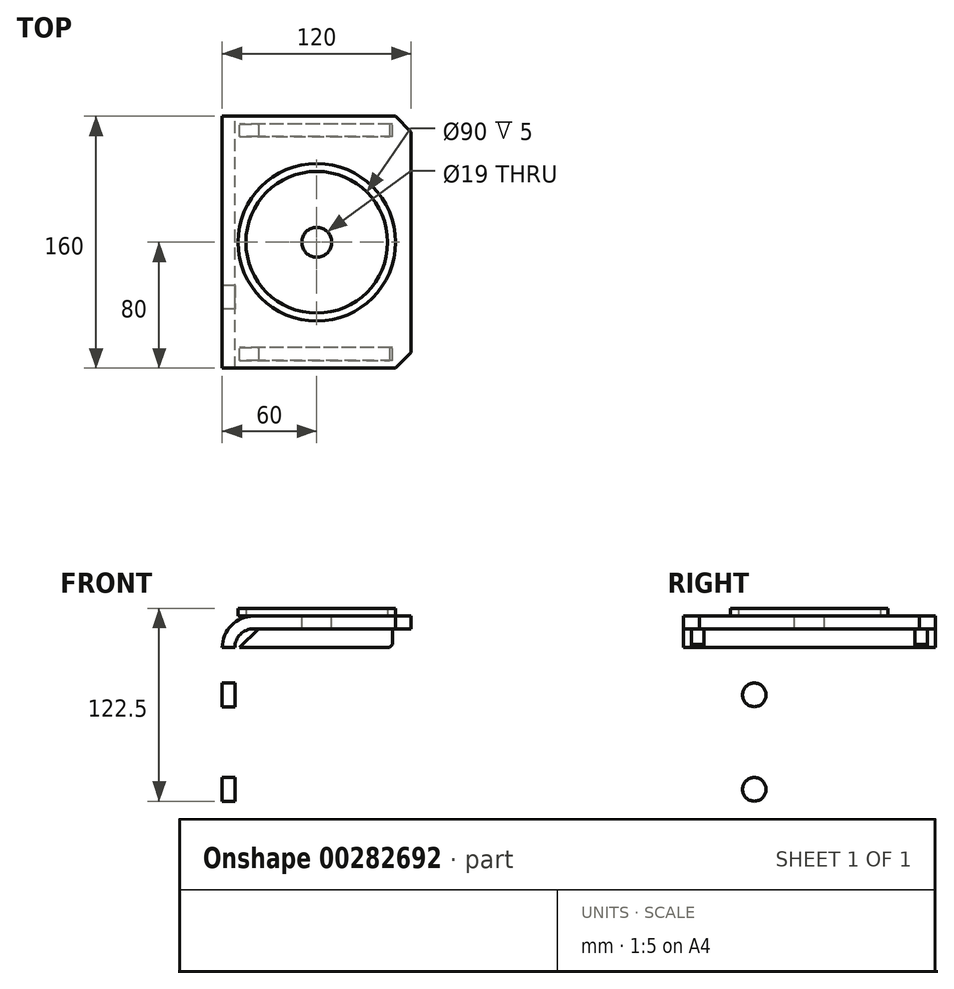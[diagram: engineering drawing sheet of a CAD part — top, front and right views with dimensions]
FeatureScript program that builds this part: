
annotation { "Feature Type Name" : "Feature", "Feature Type Description" : "" }
export const myFeature = defineFeature(function(context is Context, id is Id, definition is map)
    precondition{}
    {
        {
            var Q0;
            Q0=qCreatedBy(makeId("Front.planeOp"),FACE);
            var sketch = newSketch(context, id + "F0", { "sketchPlane" : qUnion([Q0])});
            skLineSegment(sketch, "E0", {"start": v(0, 0) * mm, "end": v(0, 120) * mm});
            skLineSegment(sketch, "E1", {"start": v(20, 140) * mm, "end": v(120, 140) * mm});
            skLineSegment(sketch, "E2.0", {"start": v(20, 132) * mm, "end": v(120, 132) * mm});
            skLineSegment(sketch, "E2.1", {"start": v(8, 0) * mm, "end": v(8, 120) * mm});
            skLineSegment(sketch, "E3", {"start": v(120, 140) * mm, "end": v(120, 132) * mm});
            skLineSegment(sketch, "E4", {"start": v(0, 0) * mm, "end": v(8, 0) * mm});
            skPoint(sketch, "E5.visualSharp", {"position": v(8, 132) * mm});
            skArc(sketch, "E5.filletArc", {"start": v(20, 132) * mm, "mid": v(11.51, 128.49) * mm, "end": v(8, 120) * mm});
            skPoint(sketch, "E6.visualSharp", {"position": v(0, 140) * mm});
            skArc(sketch, "E6.filletArc", {"start": v(20, 140) * mm, "mid": v(5.86, 134.14) * mm, "end": v(0, 120) * mm});
            skSolve(sketch);
        }
        {
            var Q0;
            Q0=makeQuery(id+"F0.imprint","IMPRINT",FACE,{"disambiguationData":[TD([[makeQuery(id+"F0.imprint","IMPRINT",EDGE,{"derivedFrom":sQuery(id+"F0.wireOp",EDGE,"E0")}),-1.0]])]});
            extrude(context, id + "F1", {"entities" : qUnion([Q0]), "depth" : 160 * mm, "symmetric" : true});
        }
        {
            var Q0;
            Q0=makeQuery(id+"F1.opExtrude","SWEPT_FACE",FACE,{"disambiguationData":[OSD([sQuery(id+"F0.wireOp",EDGE,"E2.1")])]});
            var sketch = newSketch(context, id + "F2", { "sketchPlane" : qUnion([Q0])});
            skLineSegment(sketch, "E7.0", {"start": v(-75, 132) * mm, "end": v(-67, 132) * mm});
            skLineSegment(sketch, "E8", {"start": v(-75, 132) * mm, "end": v(-75, 12) * mm});
            skLineSegment(sketch, "E9", {"start": v(-75, 12) * mm, "end": v(-67, 12) * mm});
            skLineSegment(sketch, "E10", {"start": v(-67, 12) * mm, "end": v(-67, 132) * mm});
            skLineSegment(sketch, "E11", {"start": v(67, 132) * mm, "end": v(67, 12) * mm});
            skLineSegment(sketch, "E12", {"start": v(67, 12) * mm, "end": v(75, 12) * mm});
            skLineSegment(sketch, "E13", {"start": v(75, 12) * mm, "end": v(75, 132) * mm});
            skPoint(sketch, "E14.orphan", {"position": v(-80, 132) * mm});
            skLineSegment(sketch, "E15.trimOffspring", {"start": v(67, 132) * mm, "end": v(75, 132) * mm});
            skPoint(sketch, "E16.orphan", {"position": v(80, 132) * mm});
            skSolve(sketch);
        }
        {
            var Q0;
            {var subQ0=sQuery(id+"F2.wireOp",EDGE,"E9");Q0=makeQuery(id+"F2.imprint","IMPRINT",FACE,{"disambiguationData":[TD([[makeQuery(id+"F2.imprint","IMPRINT",EDGE,{"derivedFrom":subQ0}),1.0]])]});}
            var Q1;
            {var subQ0=sQuery(id+"F2.wireOp",EDGE,"E12");Q1=makeQuery(id+"F2.imprint","IMPRINT",FACE,{"disambiguationData":[TD([[makeQuery(id+"F2.imprint","IMPRINT",EDGE,{"derivedFrom":subQ0}),1.0]])]});}
            var Q2;
            {var subQ0=sQuery(id+"F2.wireOp",EDGE,"E7.0");Q2=makeQuery(id+"F2.imprint","IMPRINT",FACE,{"disambiguationData":[TD([[makeQuery(id+"F2.imprint","IMPRINT",EDGE,{"derivedFrom":subQ0}),-1.0]])]});}
            var Q3;
            {var subQ0=sQuery(id+"F2.wireOp",EDGE,"E15.trimOffspring");Q3=makeQuery(id+"F2.imprint","IMPRINT",FACE,{"disambiguationData":[TD([[makeQuery(id+"F2.imprint","IMPRINT",EDGE,{"derivedFrom":subQ0}),-1.0]])]});}
            extrude(context, id + "F3", {"entities" : qUnion([Q0, Q1, Q2, Q3]), "depth" : 100 * mm});
        }
        {
            var Q0;
            Q0=makeQuery(id+"F3.opExtrude","CAP_EDGE",EDGE,{"disambiguationData":[OSD([sQuery(id+"F2.wireOp",EDGE,"E15.trimOffspring")])],"isStart":true});
            var Q1;
            Q1=makeQuery(id+"F3.opExtrude","CAP_EDGE",EDGE,{"disambiguationData":[OSD([sQuery(id+"F2.wireOp",EDGE,"E7.0")])],"isStart":true});
            chamfer(context, id + "F4", {"entities" : qUnion([Q0, Q1]), "width" : 15 * mm, "tangentPropagation" : true});
        }
        {
            var Q0;
            Q0=makeQuery(id+"F3.opExtrude","SWEPT_FACE",FACE,{"disambiguationData":[OSD([sQuery(id+"F2.wireOp",EDGE,"E13")])]});
            var sketch = newSketch(context, id + "F5", { "sketchPlane" : qUnion([Q0])});
            skLineSegment(sketch, "E17", {"start": v(-108, 122) * mm, "end": v(-18, 12) * mm});
            skSolve(sketch);
        }
        {
            var Q0;
            {var subQ0=sQuery(id+"F5.wireOp",EDGE,"E17");Q0=makeQuery(id+"F5.imprint","IMPRINT",FACE,{"disambiguationData":[TD([[makeQuery(id+"F5.imprint","IMPRINT",EDGE,{"derivedFrom":subQ0}),-1.0]])]});}
            extrude(context, id + "F6", {"entities" : qUnion([Q0]), "operationType" : NewBodyOperationType.REMOVE, "endBound" : BoundingType.THROUGH_ALL, "oppositeDirection" : true, "depth" : 25 * mm});
        }
        {
            var Q0;
            Q0=makeQuery(id+"F1.opExtrude","SWEPT_FACE",FACE,{"disambiguationData":[OSD([sQuery(id+"F0.wireOp",EDGE,"E1")])]});
            var sketch = newSketch(context, id + "F7", { "sketchPlane" : qUnion([Q0])});
            skLineSegment(sketch, "E18", {"start": v(0, 0) * mm, "end": v(154.98, 0) * mm, "construction": true});
            skPoint(sketch, "E18.endSnap0", {"position": v(20, 0) * mm});
            skCircle(sketch, "E19", {"center": v(60, 0) * mm, "radius": 9.5 * mm});
            skCircle(sketch, "E20", {"center": v(60, 0) * mm, "radius": 45 * mm});
            skCircle(sketch, "E21", {"center": v(60, 0) * mm, "radius": 50 * mm});
            skSolve(sketch);
        }
        {
            var Q0;
            Q0=makeQuery(id+"F7.imprint","IMPRINT",FACE,{"disambiguationData":[TD([[makeQuery(id+"F7.imprint","IMPRINT",EDGE,{"derivedFrom":sQuery(id+"F7.wireOp",EDGE,"E19")}),1.0]])]});
            extrude(context, id + "F8", {"entities" : qUnion([Q0]), "operationType" : NewBodyOperationType.REMOVE, "endBound" : BoundingType.THROUGH_ALL, "oppositeDirection" : true, "depth" : 25 * mm});
        }
        {
            var Q0;
            Q0 = qSketchRegion(id + "F7", true);
            extrude(context, id + "F9", {"entities" : qUnion([Q0]), "depth" : 5 * mm});
        }
        {
            var Q0;
            Q0=makeQuery(id+"F1.opExtrude","CAP_EDGE",EDGE,{"disambiguationData":[OSD([sQuery(id+"F0.wireOp",EDGE,"E3")])],"isStart":false});
            var Q1;
            Q1=makeQuery(id+"F1.opExtrude","CAP_EDGE",EDGE,{"disambiguationData":[OSD([sQuery(id+"F0.wireOp",EDGE,"E4")])],"isStart":false});
            var Q2;
            Q2=makeQuery(id+"F1.opExtrude","CAP_EDGE",EDGE,{"disambiguationData":[OSD([sQuery(id+"F0.wireOp",EDGE,"E3")])],"isStart":true});
            var Q3;
            Q3=makeQuery(id+"F1.opExtrude","CAP_EDGE",EDGE,{"disambiguationData":[OSD([sQuery(id+"F0.wireOp",EDGE,"E4")])],"isStart":true});
            chamfer(context, id + "F10", {"entities" : qUnion([Q0, Q1, Q2, Q3]), "width" : 10 * mm, "tangentPropagation" : true});
        }
        {
            var Q0;
            Q0=makeQuery(id+"F1.opExtrude","SWEPT_FACE",FACE,{"disambiguationData":[OSD([sQuery(id+"F0.wireOp",EDGE,"E0")])]});
            var sketch = newSketch(context, id + "F11", { "sketchPlane" : qUnion([Q0])});
            skLineSegment(sketch, "E22", {"start": v(0, 0) * mm, "end": v(0, 116.68) * mm, "construction": true});
            skCircle(sketch, "E23", {"center": v(-35, 90) * mm, "radius": 7.5 * mm});
            skCircle(sketch, "E24.MirrorC", {"center": v(35, 90) * mm, "radius": 7.5 * mm});
            skCircle(sketch, "E25.0.1.0", {"center": v(-35, 30) * mm, "radius": 7.5 * mm});
            skCircle(sketch, "E25.0.1.1", {"center": v(35, 30) * mm, "radius": 7.5 * mm});
            skLineSegment(sketch, "E25.direction1", {"start": v(-35, 90) * mm, "end": v(-10, 90) * mm, "construction": true});
            skLineSegment(sketch, "E25.direction2", {"start": v(-35, 90) * mm, "end": v(-35, 30) * mm, "construction": true});
            skSolve(sketch);
        }
        {
            var Q0;
            Q0=makeQuery(id+"F11.imprint","IMPRINT",FACE,{"disambiguationData":[TD([[makeQuery(id+"F11.imprint","IMPRINT",EDGE,{"derivedFrom":sQuery(id+"F11.wireOp",EDGE,"E23")}),1.0]])]});
            var Q1;
            Q1=makeQuery(id+"F11.imprint","IMPRINT",FACE,{"disambiguationData":[TD([[makeQuery(id+"F11.imprint","IMPRINT",EDGE,{"derivedFrom":sQuery(id+"F11.wireOp",EDGE,"E24.MirrorC")}),-1.0]])]});
            var Q2;
            Q2=makeQuery(id+"F11.imprint","IMPRINT",FACE,{"disambiguationData":[TD([[makeQuery(id+"F11.imprint","IMPRINT",EDGE,{"derivedFrom":sQuery(id+"F11.wireOp",EDGE,"E25.0.1.1")}),-1.0]])]});
            var Q3;
            Q3=makeQuery(id+"F11.imprint","IMPRINT",FACE,{"disambiguationData":[TD([[makeQuery(id+"F11.imprint","IMPRINT",EDGE,{"derivedFrom":sQuery(id+"F11.wireOp",EDGE,"E25.0.1.0")}),1.0]])]});
            extrude(context, id + "F12", {"entities" : qUnion([Q0, Q1, Q2, Q3]), "operationType" : NewBodyOperationType.REMOVE, "oppositeDirection" : true, "depth" : 25 * mm});
        }
        {
            var Q0;
            Q0=makeQuery(id+"F11.imprint","IMPRINT",FACE,{"disambiguationData":[TD([[makeQuery(id+"F11.imprint","IMPRINT",EDGE,{"derivedFrom":sQuery(id+"F11.wireOp",EDGE,"E23")}),1.0]])]});
            var Q1;
            Q1=makeQuery(id+"F11.imprint","IMPRINT",FACE,{"disambiguationData":[TD([[makeQuery(id+"F11.imprint","IMPRINT",EDGE,{"derivedFrom":sQuery(id+"F11.wireOp",EDGE,"E24.MirrorC")}),-1.0]])]});
            extrude(context, id + "F13", {"entities" : qUnion([Q0, Q1]), "operationType" : NewBodyOperationType.REMOVE, "endBound" : BoundingType.THROUGH_ALL, "oppositeDirection" : true, "depth" : 25 * mm});
        }
    });
